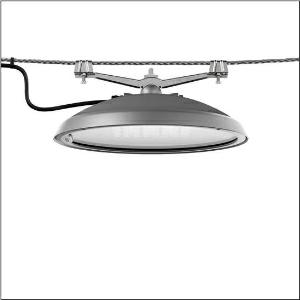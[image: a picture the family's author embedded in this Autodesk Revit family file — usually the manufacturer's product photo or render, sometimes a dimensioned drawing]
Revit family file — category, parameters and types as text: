
# Revit family: dl_r__50_iq_mini___st0_8s_5xa248v41f08fe_e25f
name_source: partatom
category: Lighting Fixtures
units: mm (PartAtom-declared; Revit-internal decimal feet)

## family parameters
Cut with Voids When Loaded = No
Host = Face
Light Source = No
Part Type = Normal
Room Calculation Point = No
Round Connector Dimension = Use Diameter
Shared = No

## types (1)
- --- (1 x LED, 2690 lm, 15.7 W, 4000K)
    Apparent Load = 16 VA
    CIE Flux Codes = 38 75 97 100 100
    Color Rendering = 70
    Color Temperature = 4000K
    Default Elevation = 1800 mm
    Description = DL® 50 iQ mini, catenary luminaire, primary light control with lens, of PMMA, primary optical cover: cover, of toughened safety glass, transparent, light distribution: ST0.8s, light emission: direct distribution, primary light characteristic: symmetric, installation type: suspended mounting, LED, High Power LED, rated luminous flux: 2.690lm, luminous efficacy: 171lm/W, light colour: 740, colour temperature: 4000K, control: optimised constant luminous flux control (CLO 2.0), Desk-Remote (wireless, voltage-free reading and setting of iQ features in the workshop via application-optimized NFC function/RFID function), Light-Fading, Smart-Wire, Night-Set, Lumen-Switch, Temp-Guard, Auto-Match, Street-Remote, mains connection: 230..240V, AC, 50/60Hz, start of lifetime: 16W, end of service life: 16W, reduction: 8W, luminaire housing, of diecast aluminium, powder-coated, Siteco® metallic grey (DB 702S), diameter: 500mm, height: 115mm, protection rating (complete): IP66, insulation class (complete): insulation class II (safety insulation), certification: CE, ENEC, VDE, impact resistance: IK08, permissible operating ambient temperature for outdoor applications: -25..+40°C, standard-compliant lighting for roads and squares, packaging unit: 1 piece

Light Distribution: ST0.8s
    Height = 124 mm
    Lamp = 1 x LED
    Lamp Light Flux = 2690 lm
    Lamp Power = 15.7 W
    Lamp count = 1
    Length = 500 mm
    Luminous efficacy = 171 lm/W
    Manufacturer = Siteco
    ModVariant = No
    Model = 5XA248V41F08FE
    Number of Poles = 1
    OnlyDefault = Yes
    Power Factor = 1
    Product Name = DL® 50 iQ mini | ST0.8s
    Product group = catenary luminaire
    ProductGroupID = 6300
    Protection Class = Protection class II
    Protection Degree = IP 66
    RLX_Detail_Level = 1
    RLX_Emergency_Light_Flux = 0 lm
    RLX_Emergency_Type = 0
    RLX_Emergency_Type_DB = No
    RlxData = <blob elided: 123113 chars, md5=9d5516c6>
    Socket = socket
    Standby Power = 0 W
    System Light Flux = 2690 lm
    System Power = 16 W
    Type Comments = factory setting: luminous flux: 100 % | dim-lin: 254 | 319 mA
    Type Image = l_1242791.jpg
    URL = http://relux.com
    VarID = @adj_069257
    Voltage = 0 V
    Weight = 0.00 kg
    Width = 0 mm  [stored 0 ft]

note: [stored X ft] marks values corroborated as IEEE doubles in the binary element streams (Revit-internal decimal feet)

## geometry (parser evidence)
native form markers: Blend x4, Sweep x12
no freeform markers — native parametric forms only
